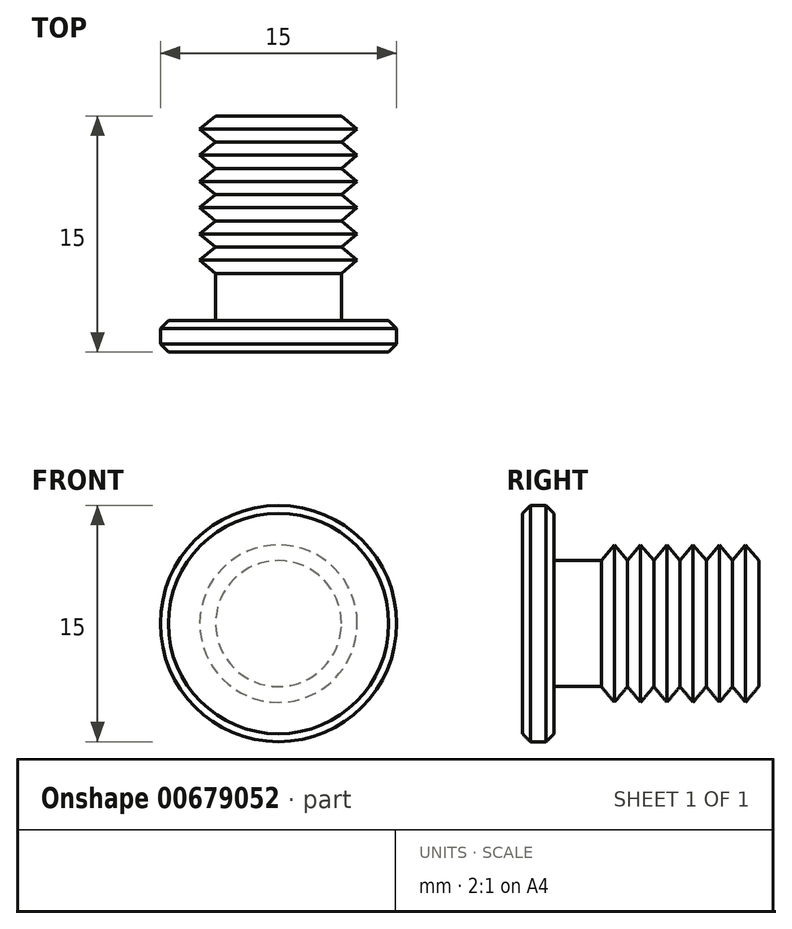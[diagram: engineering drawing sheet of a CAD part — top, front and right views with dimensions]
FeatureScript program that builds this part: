
annotation { "Feature Type Name" : "Feature", "Feature Type Description" : "" }
export const myFeature = defineFeature(function(context is Context, id is Id, definition is map)
    precondition{}
    {
        {
            var Q0;
            Q0=qCreatedBy(makeId("Top.planeOp"),FACE);
            var sketch = newSketch(context, id + "F0", { "sketchPlane" : qUnion([Q0])});
            skLineSegment(sketch, "E0", {"start": v(0, 0) * mm, "end": v(0, 32.75) * mm, "construction": true});
            skLineSegment(sketch, "E1", {"start": v(0, 0) * mm, "end": v(7, 0) * mm});
            skLineSegment(sketch, "E2", {"start": v(7, 0) * mm, "end": v(7.5, 0.5) * mm});
            skLineSegment(sketch, "E3", {"start": v(7.5, 0.5) * mm, "end": v(7.5, 1.5) * mm});
            skLineSegment(sketch, "E4", {"start": v(7.5, 1.5) * mm, "end": v(7, 2) * mm});
            skLineSegment(sketch, "E5", {"start": v(7, 2) * mm, "end": v(4, 2) * mm});
            skLineSegment(sketch, "E6", {"start": v(4, 2) * mm, "end": v(4, 5) * mm});
            skLineSegment(sketch, "E7", {"start": v(4, 5) * mm, "end": v(5, 5.83) * mm});
            skLineSegment(sketch, "E8", {"start": v(5, 5.83) * mm, "end": v(4, 6.67) * mm});
            skLineSegment(sketch, "E9", {"start": v(4, 6.67) * mm, "end": v(5, 7.5) * mm});
            skLineSegment(sketch, "E10", {"start": v(5, 7.5) * mm, "end": v(4, 8.33) * mm});
            skLineSegment(sketch, "E11", {"start": v(4, 8.33) * mm, "end": v(5, 9.17) * mm});
            skLineSegment(sketch, "E12", {"start": v(5, 9.17) * mm, "end": v(4, 10) * mm});
            skLineSegment(sketch, "E13", {"start": v(4, 10) * mm, "end": v(5, 10.83) * mm});
            skLineSegment(sketch, "E14", {"start": v(5, 10.83) * mm, "end": v(4, 11.67) * mm});
            skLineSegment(sketch, "E15", {"start": v(4, 11.67) * mm, "end": v(5, 12.5) * mm});
            skLineSegment(sketch, "E16", {"start": v(5, 12.5) * mm, "end": v(4, 13.33) * mm});
            skLineSegment(sketch, "E17", {"start": v(4, 13.33) * mm, "end": v(5, 14.17) * mm});
            skLineSegment(sketch, "E18", {"start": v(5, 14.17) * mm, "end": v(4, 15) * mm});
            skLineSegment(sketch, "E19", {"start": v(4, 15) * mm, "end": v(0, 15) * mm});
            skLineSegment(sketch, "E20", {"start": v(0, 15) * mm, "end": v(0, 0) * mm});
            skSolve(sketch);
        }
        {
            var Q0;
            Q0=qSketchRegion(id+"F0",true);
            var Q1;
            Q1=sQuery(id+"F0.wireOp",EDGE,"E0");
            revolve(context, id + "F1", {"entities" : qUnion([Q0]), "axis" : qUnion([Q1]), "revolveType" : RevolveType.FULL});
        }
    });
